# Revit family: PRD_FrankeWS_WlHngWshBsns_AnimaTrapCover_ANMX210
name_source: partatom
category: Furniture
revit_build: Autodesk Revit 2018 (Build: 20190510_1515(x64)
units: mm (PartAtom-declared; Revit-internal decimal feet)

## family parameters
Cut with Voids When Loaded = No
Host = Face
OmniClass Number = 23.40.20.21
OmniClass Title = Toilet and Bath Specialties
Room Calculation Point = No
Shared = No

## types (1)
- ANMX210
    AssetType = Fixed
    BIMObjectName = PRD_AR_WallHungWashBasins_AnimaTrapCover_ANMX210
    Category = Pr_40_20_96_96, Wall-hung wash basins
    Color = Stainless steel
    Default Elevation = 700 mm  [stored 2.29659 ft]
    Description = Wall mounted trap cover for wash basin WT600C, stainless steel, surface satin finished, material thickness 1 mm, not closed at bottom, incl. screws, dowels and brackets.
    DurationUnit = year
    Features = stainless steel, 1.00 mm, satin finished, wall mounting, 160x401x322 mm (WxHxD)
    Finish = Satin finished
    GrossWeight = 3.50 kg
    IfcExportAs = IfcFurnitureType
    IfcExportType = NOTDEFINED
    MainColor = Stainless steel
    Manufacturer = KWC Group AG
    ManufacturerName = KWC Group AG
    ManufacturerURL = www.kwc.com
    Material = Stainless steel 1.4301
    Model = ANMX210
    ModelNumber = 2000056723
    ModelReference = ANMX210
    NBSDescription = Wall hung wash basins
    NBSReference = 45-35-70/369
    Name = ANIMA trap cover ANMX210
    NetWeight = 2.70 kg
    NominalDepth = 322 mm  [stored 1.05643 ft]
    NominalHeight = 401 mm  [stored 1.31562 ft]
    NominalLength = 160 mm  [stored 0.524934 ft]
    NominalWidth = 0 mm  [stored 0 ft]
    ProductInformation = https://pim.kwc.com
    Size = 160 x 401 x 322 mm
    Style = Trap cover
    TrapCoverMaterial = PRD_AR_StainlessSteel_SatinFinished
    URL = www.kwc.com
    Uniclass2015Code = Pr_40_20_96_96
    Uniclass2015Title = Wall-hung wash basins
    Uniclass2015Version = Products v1.5
    Version = 1
    WarrantyDurationUnit = year

note: [stored X ft] marks values corroborated as IEEE doubles in the binary element streams (Revit-internal decimal feet)

## geometry (parser evidence)
native form markers: Sweep x2
no freeform markers — native parametric forms only
